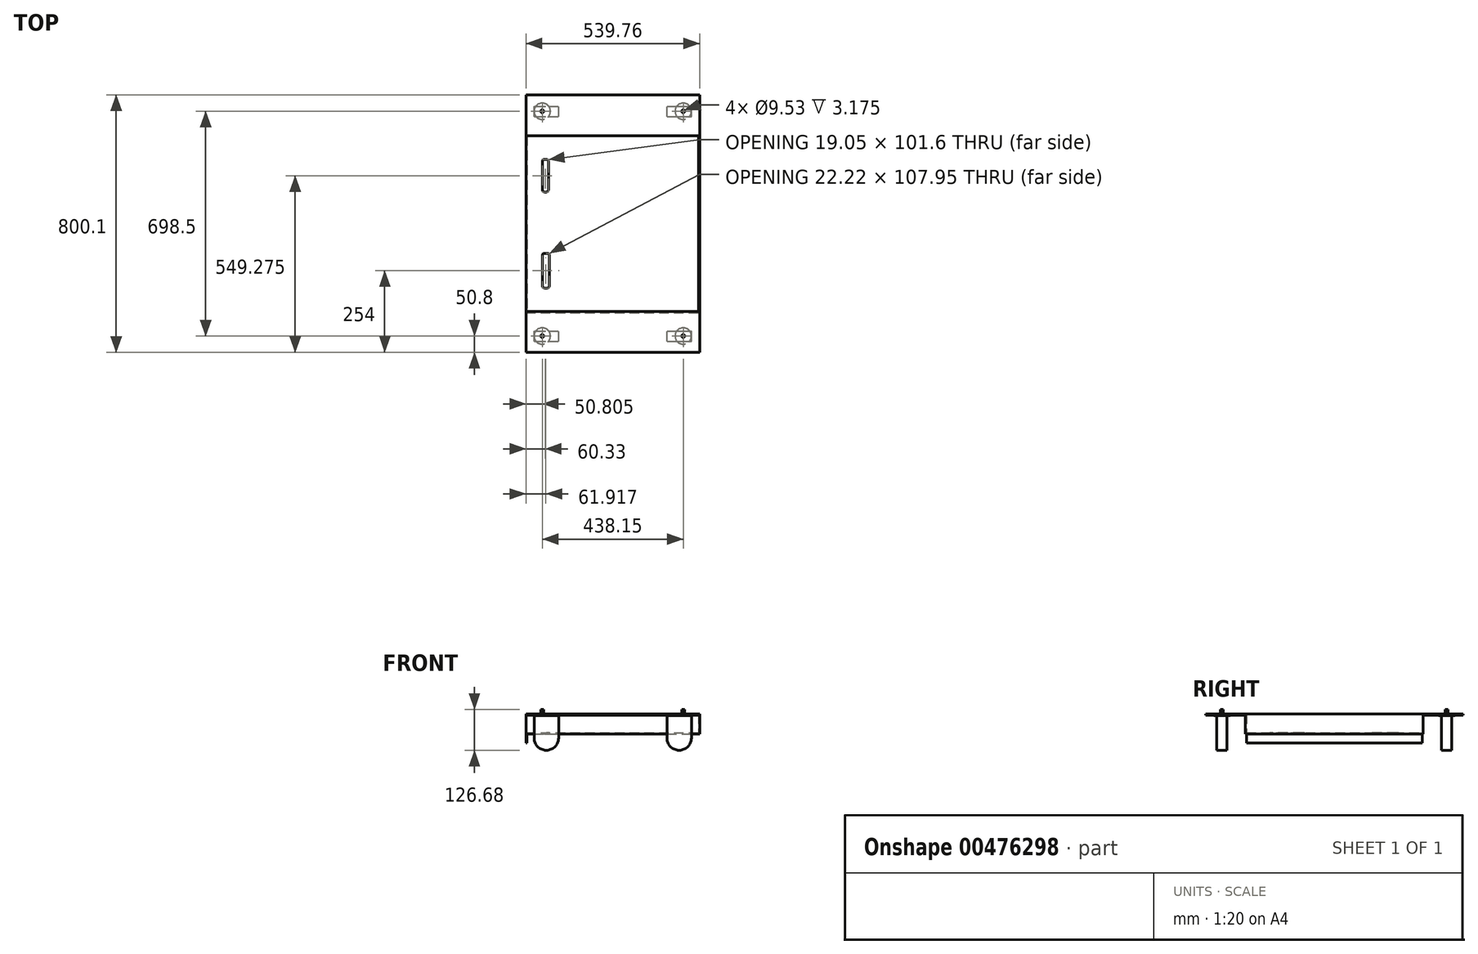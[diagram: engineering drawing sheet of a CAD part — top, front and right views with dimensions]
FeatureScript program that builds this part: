
annotation { "Feature Type Name" : "Feature", "Feature Type Description" : "" }
export const myFeature = defineFeature(function(context is Context, id is Id, definition is map)
    precondition{}
    {
        {
            var Q0;
            Q0=qCreatedBy(makeId("Top.planeOp"),FACE);
            var sketch = newSketch(context, id + "F0", { "sketchPlane" : qUnion([Q0])});
            skLineSegment(sketch, "E0.bottom", {"start": v(-269.88, 276.23) * mm, "end": v(269.88, 276.23) * mm});
            skLineSegment(sketch, "E0.top", {"start": v(-269.88, -276.23) * mm, "end": v(269.88, -276.23) * mm});
            skLineSegment(sketch, "E0.left", {"start": v(-269.88, 276.23) * mm, "end": v(-269.88, -276.23) * mm});
            skLineSegment(sketch, "E0.right", {"start": v(269.88, 276.23) * mm, "end": v(269.88, -276.23) * mm});
            skLineSegment(sketch, "E1", {"start": v(-269.88, 276.23) * mm, "end": v(269.88, -276.23) * mm, "construction": true});
            skPoint(sketch, "E2", {"position": v(0, 0) * mm});
            skLineSegment(sketch, "E3.bottom", {"start": v(-212.72, 200.03) * mm, "end": v(-206.37, 200.03) * mm});
            skLineSegment(sketch, "E3.top", {"start": v(-212.72, 98.42) * mm, "end": v(-206.37, 98.42) * mm});
            skLineSegment(sketch, "E3.left", {"start": v(-219.07, 193.68) * mm, "end": v(-219.07, 104.77) * mm});
            skLineSegment(sketch, "E3.right", {"start": v(-200.02, 193.68) * mm, "end": v(-200.02, 104.77) * mm});
            skLineSegment(sketch, "E4.bottom", {"start": v(-212.72, -92.07) * mm, "end": v(-203.2, -92.07) * mm});
            skLineSegment(sketch, "E4.top", {"start": v(-212.72, -200.03) * mm, "end": v(-203.2, -200.03) * mm});
            skLineSegment(sketch, "E4.left", {"start": v(-219.07, -98.42) * mm, "end": v(-219.07, -193.68) * mm});
            skLineSegment(sketch, "E4.right", {"start": v(-196.85, -98.42) * mm, "end": v(-196.85, -193.68) * mm});
            skPoint(sketch, "E5.visualSharp", {"position": v(-219.07, 200.03) * mm});
            skArc(sketch, "E5.filletArc", {"start": v(-212.72, 200.03) * mm, "mid": v(-217.22, 198.17) * mm, "end": v(-219.07, 193.68) * mm});
            skPoint(sketch, "E6.visualSharp", {"position": v(-200.02, 200.03) * mm});
            skArc(sketch, "E6.filletArc", {"start": v(-200.03, 193.68) * mm, "mid": v(-201.88, 198.17) * mm, "end": v(-206.37, 200.02) * mm});
            skPoint(sketch, "E7.visualSharp", {"position": v(-219.07, 98.42) * mm});
            skArc(sketch, "E7.filletArc", {"start": v(-219.07, 104.77) * mm, "mid": v(-217.22, 100.28) * mm, "end": v(-212.72, 98.43) * mm});
            skPoint(sketch, "E8.visualSharp", {"position": v(-200.02, 98.42) * mm});
            skArc(sketch, "E8.filletArc", {"start": v(-206.37, 98.43) * mm, "mid": v(-201.88, 100.28) * mm, "end": v(-200.03, 104.77) * mm});
            skPoint(sketch, "E9.visualSharp", {"position": v(-196.85, -200.03) * mm});
            skArc(sketch, "E9.filletArc", {"start": v(-203.2, -200.03) * mm, "mid": v(-198.7, -198.17) * mm, "end": v(-196.85, -193.68) * mm});
            skPoint(sketch, "E10.visualSharp", {"position": v(-219.07, -200.03) * mm});
            skArc(sketch, "E10.filletArc", {"start": v(-219.07, -193.68) * mm, "mid": v(-217.22, -198.17) * mm, "end": v(-212.72, -200.02) * mm});
            skPoint(sketch, "E11.visualSharp", {"position": v(-219.07, -92.07) * mm});
            skArc(sketch, "E11.filletArc", {"start": v(-212.72, -92.07) * mm, "mid": v(-217.22, -93.93) * mm, "end": v(-219.07, -98.42) * mm});
            skPoint(sketch, "E12.visualSharp", {"position": v(-196.85, -92.07) * mm});
            skArc(sketch, "E12.filletArc", {"start": v(-196.85, -98.42) * mm, "mid": v(-198.7, -93.93) * mm, "end": v(-203.2, -92.07) * mm});
            skSolve(sketch);
        }
        {
            var Q0;
            Q0 = qSketchRegion(id + "F0", true);
            extrude(context, id + "F1", {"entities" : qUnion([Q0]), "depth" : 3.17 * mm, "offsetDistance" : 25.4 * mm});
        }
        {
            var Q0;
            Q0=makeQuery(id+"F1.opExtrude","CAP_FACE",FACE,{"disambiguationData":[OSD([sQuery(id+"F0.wireOp",EDGE,"E0.bottom"),sQuery(id+"F0.wireOp",EDGE,"E0.top"),sQuery(id+"F0.wireOp",EDGE,"E0.left"),sQuery(id+"F0.wireOp",EDGE,"E0.right"),sQuery(id+"F0.wireOp",EDGE,"E3.bottom"),sQuery(id+"F0.wireOp",EDGE,"E3.top"),sQuery(id+"F0.wireOp",EDGE,"E3.left"),sQuery(id+"F0.wireOp",EDGE,"E3.right"),sQuery(id+"F0.wireOp",EDGE,"E4.bottom"),sQuery(id+"F0.wireOp",EDGE,"E4.top"),sQuery(id+"F0.wireOp",EDGE,"E4.left"),sQuery(id+"F0.wireOp",EDGE,"E4.right"),sQuery(id+"F0.wireOp",EDGE,"E5.filletArc"),sQuery(id+"F0.wireOp",EDGE,"E6.filletArc"),sQuery(id+"F0.wireOp",EDGE,"E7.filletArc"),sQuery(id+"F0.wireOp",EDGE,"E8.filletArc"),sQuery(id+"F0.wireOp",EDGE,"E9.filletArc"),sQuery(id+"F0.wireOp",EDGE,"E10.filletArc"),sQuery(id+"F0.wireOp",EDGE,"E11.filletArc"),sQuery(id+"F0.wireOp",EDGE,"E12.filletArc")])],"isStart":false});
            var sketch = newSketch(context, id + "F2", { "sketchPlane" : qUnion([Q0])});
            skLineSegment(sketch, "E13.top", {"start": v(-269.88, 273.05) * mm, "end": v(266.7, 273.05) * mm});
            skLineSegment(sketch, "E13.left", {"start": v(-269.88, 276.23) * mm, "end": v(-269.88, 273.05) * mm});
            skLineSegment(sketch, "E14.right", {"start": v(266.7, -273.05) * mm, "end": v(266.7, 273.05) * mm});
            skLineSegment(sketch, "E15.bottom", {"start": v(-269.88, -276.23) * mm, "end": v(269.88, -276.23) * mm});
            skLineSegment(sketch, "E15.top", {"start": v(-269.88, -273.05) * mm, "end": v(266.7, -273.05) * mm});
            skLineSegment(sketch, "E15.left", {"start": v(-269.88, -276.23) * mm, "end": v(-269.88, -273.05) * mm});
            skLineSegment(sketch, "E16", {"start": v(269.88, 276.23) * mm, "end": v(-269.88, 276.23) * mm});
            skLineSegment(sketch, "E17", {"start": v(269.88, 276.23) * mm, "end": v(269.88, -276.23) * mm});
            skSolve(sketch);
        }
        {
            var Q0;
            Q0 = qSketchRegion(id + "F2", true);
            extrude(context, id + "F3", {"entities" : qUnion([Q0]), "operationType" : NewBodyOperationType.ADD, "depth" : 58.74 * mm, "offsetDistance" : 25.4 * mm});
        }
        {
            var Q0;
            Q0=makeQuery(id+"F3.opExtrude","CAP_FACE",FACE,{"disambiguationData":[OSD([sQuery(id+"F2.wireOp",EDGE,"E13.top"),sQuery(id+"F2.wireOp",EDGE,"E13.left"),sQuery(id+"F2.wireOp",EDGE,"E14.right"),sQuery(id+"F2.wireOp",EDGE,"E15.bottom"),sQuery(id+"F2.wireOp",EDGE,"E15.top"),sQuery(id+"F2.wireOp",EDGE,"E15.left"),sQuery(id+"F2.wireOp",EDGE,"E16"),sQuery(id+"F2.wireOp",EDGE,"E17")])],"isStart":false});
            var sketch = newSketch(context, id + "F4", { "sketchPlane" : qUnion([Q0])});
            skLineSegment(sketch, "E18.bottom", {"start": v(-269.88, 273.05) * mm, "end": v(269.88, 273.05) * mm});
            skLineSegment(sketch, "E18.top", {"start": v(-269.88, 400.05) * mm, "end": v(269.88, 400.05) * mm});
            skLineSegment(sketch, "E18.left", {"start": v(-269.88, 273.05) * mm, "end": v(-269.88, 400.05) * mm});
            skLineSegment(sketch, "E18.right", {"start": v(269.88, 273.05) * mm, "end": v(269.88, 400.05) * mm});
            skLineSegment(sketch, "E19", {"start": v(-269.88, 0) * mm, "end": v(269.88, 0) * mm, "construction": true});
            skLineSegment(sketch, "E20.MirrorCS", {"start": v(-269.88, -400.05) * mm, "end": v(269.88, -400.05) * mm});
            skLineSegment(sketch, "E21.MirrorCS", {"start": v(-269.88, -273.05) * mm, "end": v(-269.88, -400.05) * mm});
            skLineSegment(sketch, "E22.MirrorCS", {"start": v(-269.88, -273.05) * mm, "end": v(269.88, -273.05) * mm});
            skLineSegment(sketch, "E23.MirrorCS", {"start": v(269.88, -273.05) * mm, "end": v(269.88, -400.05) * mm});
            skCircle(sketch, "E24", {"center": v(219.08, 349.25) * mm, "radius": 4.76 * mm});
            skCircle(sketch, "E25", {"center": v(-219.08, 349.25) * mm, "radius": 4.76 * mm});
            skCircle(sketch, "E26", {"center": v(-219.07, -349.25) * mm, "radius": 4.76 * mm});
            skCircle(sketch, "E27", {"center": v(219.08, -349.25) * mm, "radius": 4.76 * mm});
            skSolve(sketch);
        }
        {
            var Q0;
            Q0 = qSketchRegion(id + "F4", true);
            extrude(context, id + "F5", {"entities" : qUnion([Q0]), "operationType" : NewBodyOperationType.ADD, "oppositeDirection" : true, "depth" : 3.17 * mm, "offsetDistance" : 25.4 * mm});
        }
        {
            var Q0;
            Q0=makeQuery(id+"F5.opExtrude","CAP_FACE",FACE,{"disambiguationData":[OSD([sQuery(id+"F4.wireOp",EDGE,"E20.MirrorCS"),sQuery(id+"F4.wireOp",EDGE,"E21.MirrorCS"),sQuery(id+"F4.wireOp",EDGE,"E22.MirrorCS"),sQuery(id+"F4.wireOp",EDGE,"E23.MirrorCS"),sQuery(id+"F4.wireOp",EDGE,"E26"),sQuery(id+"F4.wireOp",EDGE,"E27")])],"isStart":false});
            var sketch = newSketch(context, id + "F6", { "sketchPlane" : qUnion([Q0])});
            skCircle(sketch, "E28", {"center": v(-219.07, 349.25) * mm, "radius": 4.7 * mm});
            skCircle(sketch, "E29", {"center": v(219.08, 349.25) * mm, "radius": 4.7 * mm});
            skCircle(sketch, "E30", {"center": v(-219.07, -349.25) * mm, "radius": 4.7 * mm});
            skCircle(sketch, "E31", {"center": v(219.08, -349.25) * mm, "radius": 4.7 * mm});
            skSolve(sketch);
        }
        {
            var Q0;
            Q0 = qSketchRegion(id + "F6", true);
            extrude(context, id + "F7", {"entities" : qUnion([Q0]), "operationType" : NewBodyOperationType.ADD, "oppositeDirection" : true, "depth" : 17.14 * mm, "offsetDistance" : 25.4 * mm});
        }
        {
            var Q0;
            Q0=makeQuery(id+"F5.opExtrude","CAP_FACE",FACE,{"disambiguationData":[OSD([sQuery(id+"F4.wireOp",EDGE,"E20.MirrorCS"),sQuery(id+"F4.wireOp",EDGE,"E21.MirrorCS"),sQuery(id+"F4.wireOp",EDGE,"E22.MirrorCS"),sQuery(id+"F4.wireOp",EDGE,"E23.MirrorCS"),sQuery(id+"F4.wireOp",EDGE,"E26"),sQuery(id+"F4.wireOp",EDGE,"E27")])],"isStart":false});
            var sketch = newSketch(context, id + "F8", { "sketchPlane" : qUnion([Q0])});
            skCircle(sketch, "E32", {"center": v(-219.07, 349.25) * mm, "radius": 25.4 * mm});
            skCircle(sketch, "E33", {"center": v(219.08, 349.25) * mm, "radius": 25.4 * mm});
            skCircle(sketch, "E34", {"center": v(-219.07, -349.25) * mm, "radius": 25.4 * mm});
            skCircle(sketch, "E35", {"center": v(219.08, -349.25) * mm, "radius": 25.4 * mm});
            skSolve(sketch);
        }
        {
            var Q0;
            Q0 = qSketchRegion(id + "F8", true);
            extrude(context, id + "F9", {"entities" : qUnion([Q0]), "operationType" : NewBodyOperationType.ADD, "depth" : 1.65 * mm, "offsetDistance" : 25.4 * mm});
        }
        {
            var Q0;
            Q0=makeQuery(id+"F9.opExtrude","CAP_FACE",FACE,{"disambiguationData":[OSD([sQuery(id+"F8.wireOp",EDGE,"E32")])],"isStart":false});
            var sketch = newSketch(context, id + "F10", { "sketchPlane" : qUnion([Q0])});
            skLineSegment(sketch, "E36.bottom", {"start": v(-244.47, 365.13) * mm, "end": v(-168.28, 365.13) * mm});
            skLineSegment(sketch, "E36.top", {"start": v(-244.47, 333.38) * mm, "end": v(-168.28, 333.38) * mm});
            skLineSegment(sketch, "E36.left", {"start": v(-244.47, 365.13) * mm, "end": v(-244.47, 333.38) * mm});
            skLineSegment(sketch, "E36.right", {"start": v(-168.28, 365.13) * mm, "end": v(-168.28, 333.38) * mm});
            skLineSegment(sketch, "E37.bottom", {"start": v(168.28, 365.13) * mm, "end": v(244.48, 365.13) * mm});
            skLineSegment(sketch, "E37.top", {"start": v(168.28, 333.38) * mm, "end": v(244.48, 333.38) * mm});
            skLineSegment(sketch, "E37.left", {"start": v(168.28, 365.13) * mm, "end": v(168.28, 333.38) * mm});
            skLineSegment(sketch, "E37.right", {"start": v(244.48, 365.13) * mm, "end": v(244.48, 333.38) * mm});
            skLineSegment(sketch, "E38.bottom", {"start": v(-244.47, -333.38) * mm, "end": v(-168.27, -333.38) * mm});
            skLineSegment(sketch, "E38.top", {"start": v(-244.47, -365.13) * mm, "end": v(-168.27, -365.13) * mm});
            skLineSegment(sketch, "E38.left", {"start": v(-244.47, -333.38) * mm, "end": v(-244.47, -365.13) * mm});
            skLineSegment(sketch, "E38.right", {"start": v(-168.27, -333.38) * mm, "end": v(-168.27, -365.13) * mm});
            skLineSegment(sketch, "E39.bottom", {"start": v(168.28, -333.38) * mm, "end": v(244.48, -333.38) * mm});
            skLineSegment(sketch, "E39.top", {"start": v(168.28, -365.13) * mm, "end": v(244.48, -365.13) * mm});
            skLineSegment(sketch, "E39.left", {"start": v(168.28, -333.38) * mm, "end": v(168.28, -365.13) * mm});
            skLineSegment(sketch, "E39.right", {"start": v(244.48, -333.38) * mm, "end": v(244.48, -365.13) * mm});
            skLineSegment(sketch, "E40", {"start": v(-244.47, 349.25) * mm, "end": v(-168.28, 349.25) * mm, "construction": true});
            skLineSegment(sketch, "E41", {"start": v(168.28, 349.25) * mm, "end": v(244.48, 349.25) * mm, "construction": true});
            skLineSegment(sketch, "E42", {"start": v(-244.47, -349.25) * mm, "end": v(-168.27, -349.25) * mm, "construction": true});
            skLineSegment(sketch, "E43", {"start": v(168.28, -349.25) * mm, "end": v(244.48, -349.25) * mm, "construction": true});
            skSolve(sketch);
        }
        {
            var Q0;
            Q0 = qSketchRegion(id + "F10", true);
            extrude(context, id + "F11", {"entities" : qUnion([Q0]), "operationType" : NewBodyOperationType.ADD, "depth" : 107.89 * mm, "offsetDistance" : 25.4 * mm});
        }
        {
            var Q0;
            Q0=makeQuery(id+"F11.opExtrude","CAP_EDGE",EDGE,{"disambiguationData":[OSD([sQuery(id+"F10.wireOp",EDGE,"E36.right")])],"isStart":false});
            var Q1;
            Q1=makeQuery(id+"F11.opExtrude","CAP_EDGE",EDGE,{"disambiguationData":[OSD([sQuery(id+"F10.wireOp",EDGE,"E36.left")])],"isStart":false});
            var Q2;
            Q2=makeQuery(id+"F11.opExtrude","CAP_EDGE",EDGE,{"disambiguationData":[OSD([sQuery(id+"F10.wireOp",EDGE,"E37.left")])],"isStart":false});
            var Q3;
            Q3=makeQuery(id+"F11.opExtrude","CAP_EDGE",EDGE,{"disambiguationData":[OSD([sQuery(id+"F10.wireOp",EDGE,"E37.right")])],"isStart":false});
            var Q4;
            Q4=makeQuery(id+"F11.opExtrude","CAP_EDGE",EDGE,{"disambiguationData":[OSD([sQuery(id+"F10.wireOp",EDGE,"E38.left")])],"isStart":false});
            var Q5;
            Q5=makeQuery(id+"F11.opExtrude","CAP_EDGE",EDGE,{"disambiguationData":[OSD([sQuery(id+"F10.wireOp",EDGE,"E38.right")])],"isStart":false});
            var Q6;
            Q6=makeQuery(id+"F11.opExtrude","CAP_EDGE",EDGE,{"disambiguationData":[OSD([sQuery(id+"F10.wireOp",EDGE,"E39.left")])],"isStart":false});
            var Q7;
            Q7=makeQuery(id+"F11.opExtrude","CAP_EDGE",EDGE,{"disambiguationData":[OSD([sQuery(id+"F10.wireOp",EDGE,"E39.right")])],"isStart":false});
            fillet(context, id + "F12", {"entities" : qUnion([Q0, Q1, Q2, Q3, Q4, Q5, Q6, Q7]), "radius" : 38.1 * mm, "tangentPropagation" : true, "allowEdgeOverflow" : false});
        }
        {
            var Q0;
            Q0=makeQuery(id+"F1.opExtrude","CAP_FACE",FACE,{"disambiguationData":[OSD([sQuery(id+"F0.wireOp",EDGE,"E0.bottom"),sQuery(id+"F0.wireOp",EDGE,"E0.top"),sQuery(id+"F0.wireOp",EDGE,"E0.left"),sQuery(id+"F0.wireOp",EDGE,"E0.right"),sQuery(id+"F0.wireOp",EDGE,"E3.bottom"),sQuery(id+"F0.wireOp",EDGE,"E3.top"),sQuery(id+"F0.wireOp",EDGE,"E3.left"),sQuery(id+"F0.wireOp",EDGE,"E3.right"),sQuery(id+"F0.wireOp",EDGE,"E4.bottom"),sQuery(id+"F0.wireOp",EDGE,"E4.top"),sQuery(id+"F0.wireOp",EDGE,"E4.left"),sQuery(id+"F0.wireOp",EDGE,"E4.right"),sQuery(id+"F0.wireOp",EDGE,"E5.filletArc"),sQuery(id+"F0.wireOp",EDGE,"E6.filletArc"),sQuery(id+"F0.wireOp",EDGE,"E7.filletArc"),sQuery(id+"F0.wireOp",EDGE,"E8.filletArc"),sQuery(id+"F0.wireOp",EDGE,"E9.filletArc"),sQuery(id+"F0.wireOp",EDGE,"E10.filletArc"),sQuery(id+"F0.wireOp",EDGE,"E11.filletArc"),sQuery(id+"F0.wireOp",EDGE,"E12.filletArc")])],"isStart":false});
            var sketch = newSketch(context, id + "F13", { "sketchPlane" : qUnion([Q0])});
            skLineSegment(sketch, "E44.bottom", {"start": v(-269.88, 273.05) * mm, "end": v(-266.7, 273.05) * mm});
            skLineSegment(sketch, "E44.top", {"start": v(-269.88, -273.05) * mm, "end": v(-266.7, -273.05) * mm});
            skLineSegment(sketch, "E44.left", {"start": v(-269.88, 273.05) * mm, "end": v(-269.88, -273.05) * mm});
            skLineSegment(sketch, "E44.right", {"start": v(-266.7, 273.05) * mm, "end": v(-266.7, -273.05) * mm});
            skSolve(sketch);
        }
        {
            var Q0;
            Q0 = qSketchRegion(id + "F13", true);
            extrude(context, id + "F14", {"entities" : qUnion([Q0]), "operationType" : NewBodyOperationType.ADD, "oppositeDirection" : true, "depth" : 31.75 * mm, "offsetDistance" : 25.4 * mm});
        }
    });
